# Revit family: FSL
name_source: partatom
category: Lighting Fixtures
units: mm (PartAtom-declared; Revit-internal decimal feet)

## family parameters
Cut with Voids When Loaded = No
Host = Face
Light Source = No
OmniClass Number = 23.80.70.14.14
OmniClass Title = Exterior Floodlights
Part Type = Normal
Room Calculation Point = No
Round Connector Dimension = Use Diameter
Shared = Yes

## types (1)
- FSL
    Apparent Load = 0 VA
    Default Elevation = 48.000"
    Description = Office buildings, monuments, facades, columns, flag poles, bridges, commercial, mixed retail, apartments, schools and campuses
    Finish = Bronze
    Lens = White Glass
    Manufacturer = EXO
    Model = FSL 10 LED Floodlight
    Photometric Web = Web ARF1 : ARF1-K-10L5K-070-W-U-DB
    Pivot Angle = 0.00°
    Pivot calc. = 90.00°
    Stand = Bronze
    Tilt Angle = 0.00°
    Total Input Wattage = 25 W
    URL = https://www.currentlighting.com
    Voltage = 120 V

## geometry (parser evidence)
native form markers: Blend x13, Sweep x8
no freeform markers — native parametric forms only
